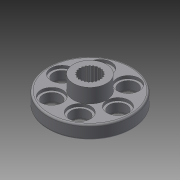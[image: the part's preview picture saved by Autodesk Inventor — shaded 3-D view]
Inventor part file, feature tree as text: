
AUTODESK INVENTOR PART (.ipt)
format: ipt  version: 2013 (Build 170138000, 138)  size: 283,136 bytes
history: native  units: mm
features: other x4, extrude x4, sketch x2, pattern_circular x2, plane x1, fillet x1, projected_geometry x1
ambient origin geometry x8: Origin, YZ Plane, XZ Plane, XY Plane, X Axis, Y Axis, Z Axis, Center Point
bodies: Solid2 (feature_tree), Solid1 (feature_tree)
feature tree (15):
  other  "baza orczyka do SRM-102 (23 teeth) do druku.ipt"
  plane  "Work Plane1"
  sketch  "Sketch1"  dims[d0=10.0mm d1=5.0mm]
  extrude  "Extrusion1"  Depth=5.0mm
  extrude  "Extrusion4"  Depth=24.0mm
  extrude  "Extrusion5"  Depth=3.9mm
  pattern_circular  "Circular Pattern2"  [2 undecoded]
  pattern_circular  "Circular Pattern3"  [2 undecoded]
  fillet  "Fillet1"  [1 undecoded]
  extrude  "support"  Depth=2.3mm TaperAngle=0.0deg
  other  "Solid1::baza orczyka do SRM-102 (23 teeth) do druku.ipt"
  other  "TaggingFeature1"
  other  "Pattern of Solid1:1"
  sketch  "Sketch3"  dims[d3=6.3mm d8=24.0mm d9=3.9mm d10=0.0mm d18=3.9mm d19=0.0mm d20=2.3mm d21=0.0mm d22=60.0mm d23=360.0deg d25=20.0mm d26=90.0deg d28=-0.45mm d33=0.5mm d34=0.05mm d35=0.0mm]
  projected_geometry  "Projected Loop1"
note: 5 required parameter values undecoded (feature->parameter linkage not recoverable at this tier; creation-order binding heuristic only, values carry confidence <= 0.55)
